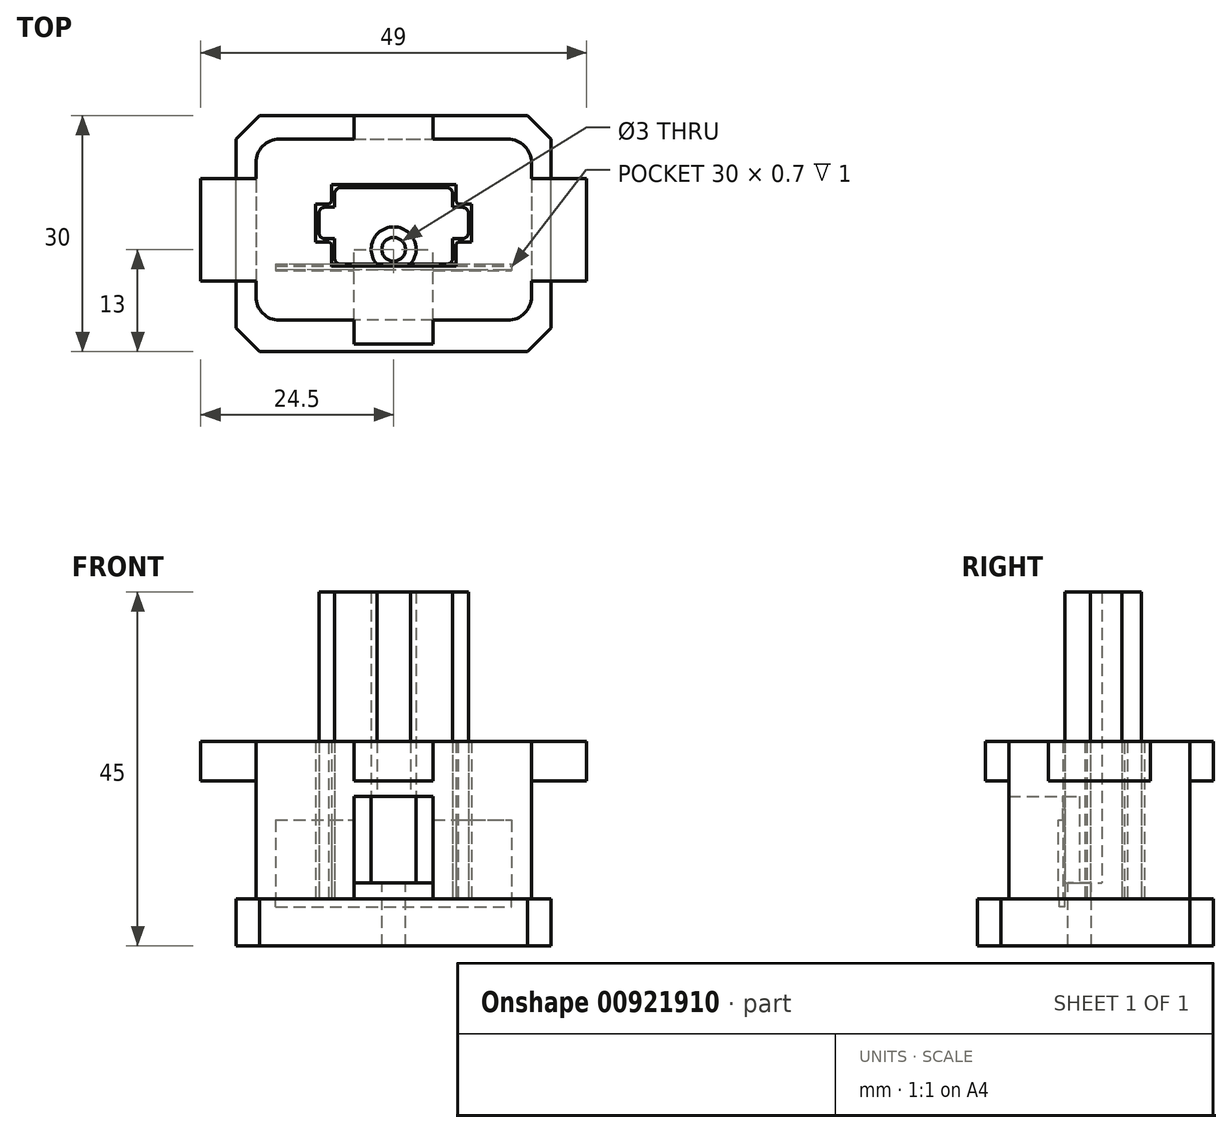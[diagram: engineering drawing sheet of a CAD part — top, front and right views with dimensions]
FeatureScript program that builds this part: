
annotation { "Feature Type Name" : "Feature", "Feature Type Description" : "" }
export const myFeature = defineFeature(function(context is Context, id is Id, definition is map)
    precondition{}
    {
        {
            var Q0;
            Q0=qCreatedBy(makeId("Top.planeOp"),FACE);
            var sketch = newSketch(context, id + "F0", { "sketchPlane" : qUnion([Q0])});
            skLineSegment(sketch, "E0.bottom", {"start": v(-7.5, 7.85) * mm, "end": v(7.5, 7.85) * mm});
            skLineSegment(sketch, "E0.top", {"start": v(-7.5, -1.9) * mm, "end": v(-2.12, -1.9) * mm});
            skLineSegment(sketch, "E0.left", {"start": v(-7.5, 7.85) * mm, "end": v(-7.5, -1.9) * mm});
            skLineSegment(sketch, "E0.right", {"start": v(7.5, 7.85) * mm, "end": v(7.5, -1.9) * mm});
            skArc(sketch, "E1", {"start": v(2.12, -1.9) * mm, "mid": v(0, 2.85) * mm, "end": v(-2.12, -1.9) * mm});
            skLineSegment(sketch, "E2.trimOffspring", {"start": v(2.12, -1.9) * mm, "end": v(7.5, -1.9) * mm});
            skSolve(sketch);
        }
        {
            var Q0;
            Q0=makeQuery(id+"F0.imprint","IMPRINT",FACE,{"disambiguationData":[TD([[makeQuery(id+"F0.imprint","IMPRINT",EDGE,{"derivedFrom":sQuery(id+"F0.wireOp",EDGE,"E0.bottom")}),-1.0]])]});
            extrude(context, id + "F1", {"entities" : qUnion([Q0]), "depth" : 39 * mm, "offsetDistance" : 25 * mm});
        }
        {
            var Q0;
            Q0=makeQuery(id+"F1.opExtrude","CAP_FACE",FACE,{"disambiguationData":[OSD([sQuery(id+"F0.wireOp",EDGE,"E0.bottom"),sQuery(id+"F0.wireOp",EDGE,"E0.top"),sQuery(id+"F0.wireOp",EDGE,"E0.left"),sQuery(id+"F0.wireOp",EDGE,"E0.right"),sQuery(id+"F0.wireOp",EDGE,"E1"),sQuery(id+"F0.wireOp",EDGE,"E2.trimOffspring")])],"isStart":true});
            var sketch = newSketch(context, id + "F2", { "sketchPlane" : qUnion([Q0])});
            skLineSegment(sketch, "E3.bottom", {"start": v(-20, 13) * mm, "end": v(20, 13) * mm});
            skLineSegment(sketch, "E3.top", {"start": v(-20, -17) * mm, "end": v(20, -17) * mm});
            skLineSegment(sketch, "E3.left", {"start": v(-20, 13) * mm, "end": v(-20, -17) * mm});
            skLineSegment(sketch, "E3.right", {"start": v(20, 13) * mm, "end": v(20, -17) * mm});
            skSolve(sketch);
        }
        {
            var Q0;
            Q0 = qSketchRegion(id + "F2", true);
            extrude(context, id + "F3", {"entities" : qUnion([Q0]), "operationType" : NewBodyOperationType.ADD, "depth" : 6 * mm, "offsetDistance" : 25 * mm});
        }
        {
            var Q0;
            Q0=makeQuery(id+"F3.opExtrude","CAP_FACE",FACE,{"disambiguationData":[OSD([sQuery(id+"F2.wireOp",EDGE,"E3.bottom"),sQuery(id+"F2.wireOp",EDGE,"E3.top"),sQuery(id+"F2.wireOp",EDGE,"E3.left"),sQuery(id+"F2.wireOp",EDGE,"E3.right")])],"isStart":true});
            var sketch = newSketch(context, id + "F4", { "sketchPlane" : qUnion([Q0])});
            skLineSegment(sketch, "E4.bottom", {"start": v(-7.5, 5.35) * mm, "end": v(-9.5, 5.35) * mm});
            skLineSegment(sketch, "E4.top", {"start": v(-7.5, 1.35) * mm, "end": v(-9.5, 1.35) * mm});
            skLineSegment(sketch, "E4.left", {"start": v(-7.5, 5.35) * mm, "end": v(-7.5, 1.35) * mm});
            skLineSegment(sketch, "E4.right", {"start": v(-9.5, 5.35) * mm, "end": v(-9.5, 1.35) * mm});
            skLineSegment(sketch, "E5.bottom", {"start": v(7.5, 5.35) * mm, "end": v(9.5, 5.35) * mm});
            skLineSegment(sketch, "E5.top", {"start": v(7.5, 1.35) * mm, "end": v(9.5, 1.35) * mm});
            skLineSegment(sketch, "E5.left", {"start": v(7.5, 5.35) * mm, "end": v(7.5, 1.35) * mm});
            skLineSegment(sketch, "E5.right", {"start": v(9.5, 5.35) * mm, "end": v(9.5, 1.35) * mm});
            skSolve(sketch);
        }
        {
            var Q0;
            Q0 = qSketchRegion(id + "F4", true);
            var Q1;
            Q1=makeQuery(id+"F1.opExtrude","CAP_FACE",FACE,{"disambiguationData":[OSD([sQuery(id+"F0.wireOp",EDGE,"E0.bottom"),sQuery(id+"F0.wireOp",EDGE,"E0.top"),sQuery(id+"F0.wireOp",EDGE,"E0.left"),sQuery(id+"F0.wireOp",EDGE,"E0.right"),sQuery(id+"F0.wireOp",EDGE,"E1"),sQuery(id+"F0.wireOp",EDGE,"E2.trimOffspring")])],"isStart":false});
            extrude(context, id + "F5", {"entities" : qUnion([Q0]), "operationType" : NewBodyOperationType.ADD, "endBound" : BoundingType.UP_TO_SURFACE, "depth" : 25 * mm, "endBoundEntityFace" : qUnion([Q1]), "offsetDistance" : 25 * mm});
        }
        {
            var Q0;
            Q0=makeQuery(id+"F1.opExtrude","SWEPT_EDGE",EDGE,{"disambiguationData":[OSD([sQuery(id+"F0.wireOp",EDGE,"E0.top"),sQuery(id+"F0.wireOp",EDGE,"E0.left")])]});
            var Q1;
            Q1=makeQuery(id+"F1.opExtrude","SWEPT_EDGE",EDGE,{"disambiguationData":[OSD([sQuery(id+"F0.wireOp",EDGE,"E0.right"),sQuery(id+"F0.wireOp",EDGE,"E2.trimOffspring")])]});
            var Q2;
            Q2=makeQuery(id+"F1.opExtrude","SWEPT_EDGE",EDGE,{"disambiguationData":[OSD([sQuery(id+"F0.wireOp",EDGE,"E0.bottom"),sQuery(id+"F0.wireOp",EDGE,"E0.right")])]});
            var Q3;
            Q3=makeQuery(id+"F1.opExtrude","SWEPT_EDGE",EDGE,{"disambiguationData":[OSD([sQuery(id+"F0.wireOp",EDGE,"E0.bottom"),sQuery(id+"F0.wireOp",EDGE,"E0.left")])]});
            var Q4;
            Q4=makeQuery(id+"F5.opExtrude","SWEPT_EDGE",EDGE,{"disambiguationData":[OSD([sQuery(id+"F4.wireOp",EDGE,"E4.bottom"),sQuery(id+"F4.wireOp",EDGE,"E4.right")])]});
            var Q5;
            Q5=makeQuery(id+"F5.opExtrude","SWEPT_EDGE",EDGE,{"disambiguationData":[OSD([sQuery(id+"F4.wireOp",EDGE,"E4.top"),sQuery(id+"F4.wireOp",EDGE,"E4.right")])]});
            var Q6;
            Q6=makeQuery(id+"F5.opExtrude","SWEPT_EDGE",EDGE,{"disambiguationData":[OSD([sQuery(id+"F4.wireOp",EDGE,"E5.top"),sQuery(id+"F4.wireOp",EDGE,"E5.right")])]});
            var Q7;
            Q7=makeQuery(id+"F5.opExtrude","SWEPT_EDGE",EDGE,{"disambiguationData":[OSD([sQuery(id+"F4.wireOp",EDGE,"E5.bottom"),sQuery(id+"F4.wireOp",EDGE,"E5.right")])]});
            fillet(context, id + "F6", {"entities" : qUnion([Q0, Q1, Q2, Q3, Q4, Q5, Q6, Q7]), "radius" : 0.8 * mm, "tangentPropagation" : true, "allowEdgeOverflow" : false});
        }
        {
            var Q0;
            Q0=makeQuery(id+"F3.opExtrude","CAP_FACE",FACE,{"disambiguationData":[OSD([sQuery(id+"F2.wireOp",EDGE,"E3.bottom"),sQuery(id+"F2.wireOp",EDGE,"E3.top"),sQuery(id+"F2.wireOp",EDGE,"E3.left"),sQuery(id+"F2.wireOp",EDGE,"E3.right")])],"isStart":true});
            var sketch = newSketch(context, id + "F7", { "sketchPlane" : qUnion([Q0])});
            skLineSegment(sketch, "E6.bottom", {"start": v(-17.5, 14) * mm, "end": v(17.5, 14) * mm});
            skLineSegment(sketch, "E6.top", {"start": v(-17.5, -9) * mm, "end": v(17.5, -9) * mm});
            skLineSegment(sketch, "E6.left", {"start": v(-17.5, 14) * mm, "end": v(-17.5, -9) * mm});
            skLineSegment(sketch, "E6.right", {"start": v(17.5, 14) * mm, "end": v(17.5, -9) * mm});
            skLineSegment(sketch, "E7.bottom", {"start": v(-7.9, 8.25) * mm, "end": v(7.9, 8.25) * mm});
            skLineSegment(sketch, "E7.top", {"start": v(-7.9, -2.1) * mm, "end": v(7.9, -2.1) * mm});
            skLineSegment(sketch, "E7.left", {"start": v(-9.9, 5.75) * mm, "end": v(-9.9, 0.95) * mm});
            skLineSegment(sketch, "E7.right", {"start": v(9.9, 5.75) * mm, "end": v(9.9, 0.95) * mm});
            skLineSegment(sketch, "E8", {"start": v(-9.9, 5.75) * mm, "end": v(-7.9, 5.75) * mm});
            skLineSegment(sketch, "E9", {"start": v(-7.9, 5.75) * mm, "end": v(-7.9, 8.25) * mm});
            skLineSegment(sketch, "E10.MirrorCS", {"start": v(9.9, 5.75) * mm, "end": v(7.9, 5.75) * mm});
            skLineSegment(sketch, "E11.MirrorCS", {"start": v(7.9, 5.75) * mm, "end": v(7.9, 8.25) * mm});
            skLineSegment(sketch, "E12", {"start": v(-9.9, 0.95) * mm, "end": v(-7.9, 0.95) * mm});
            skLineSegment(sketch, "E13", {"start": v(-7.9, 0.95) * mm, "end": v(-7.9, -2.1) * mm});
            skLineSegment(sketch, "E14.MirrorCS", {"start": v(9.9, 0.95) * mm, "end": v(7.9, 0.95) * mm});
            skLineSegment(sketch, "E15.MirrorCS", {"start": v(7.9, 0.95) * mm, "end": v(7.9, -2.1) * mm});
            skSolve(sketch);
        }
        {
            var Q0;
            Q0 = qSketchRegion(id + "F7", true);
            extrude(context, id + "F8", {"entities" : qUnion([Q0]), "depth" : 20 * mm, "offsetDistance" : 25 * mm});
        }
        {
            var Q0;
            Q0=makeQuery(id+"Fze5ySvmm35KPdi_2.boolean.opBoolean","MERGE",EDGE,{"derivedFrom":[makeQuery(id+"F8.opExtrude","SWEPT_EDGE",EDGE,{"disambiguationData":[OSD([sQuery(id+"F7.wireOp",EDGE,"E6.bottom"),sQuery(id+"F7.wireOp",EDGE,"E6.left")])]}),makeQuery(id+"Fze5ySvmm35KPdi_2.opExtrude","SWEPT_EDGE",EDGE,{"disambiguationData":[OSD([sQuery(id+"F3sfEmMIL337t9d_2.wireOp",EDGE,"Gmu0uAIl-RP7c-kK6N-eZ0a-JbMQpHXrm7wh.bottom"),sQuery(id+"F3sfEmMIL337t9d_2.wireOp",EDGE,"Gmu0uAIl-RP7c-kK6N-eZ0a-JbMQpHXrm7wh.left")])]})]});
            var Q1;
            Q1=makeQuery(id+"Fze5ySvmm35KPdi_2.boolean.opBoolean","MERGE",EDGE,{"derivedFrom":[makeQuery(id+"F8.opExtrude","SWEPT_EDGE",EDGE,{"disambiguationData":[OSD([sQuery(id+"F7.wireOp",EDGE,"E6.bottom"),sQuery(id+"F7.wireOp",EDGE,"E6.right")])]}),makeQuery(id+"Fze5ySvmm35KPdi_2.opExtrude","SWEPT_EDGE",EDGE,{"disambiguationData":[OSD([sQuery(id+"F3sfEmMIL337t9d_2.wireOp",EDGE,"Gmu0uAIl-RP7c-kK6N-eZ0a-JbMQpHXrm7wh.bottom"),sQuery(id+"F3sfEmMIL337t9d_2.wireOp",EDGE,"Gmu0uAIl-RP7c-kK6N-eZ0a-JbMQpHXrm7wh.right")])]})]});
            var Q2;
            Q2=makeQuery(id+"Fze5ySvmm35KPdi_2.boolean.opBoolean","MERGE",EDGE,{"derivedFrom":[makeQuery(id+"F8.opExtrude","SWEPT_EDGE",EDGE,{"disambiguationData":[OSD([sQuery(id+"F7.wireOp",EDGE,"E6.top"),sQuery(id+"F7.wireOp",EDGE,"E6.right")])]}),makeQuery(id+"Fze5ySvmm35KPdi_2.opExtrude","SWEPT_EDGE",EDGE,{"disambiguationData":[OSD([sQuery(id+"F3sfEmMIL337t9d_2.wireOp",EDGE,"Gmu0uAIl-RP7c-kK6N-eZ0a-JbMQpHXrm7wh.top"),sQuery(id+"F3sfEmMIL337t9d_2.wireOp",EDGE,"Gmu0uAIl-RP7c-kK6N-eZ0a-JbMQpHXrm7wh.right")])]})]});
            var Q3;
            Q3=makeQuery(id+"Fze5ySvmm35KPdi_2.boolean.opBoolean","MERGE",EDGE,{"derivedFrom":[makeQuery(id+"F8.opExtrude","SWEPT_EDGE",EDGE,{"disambiguationData":[OSD([sQuery(id+"F7.wireOp",EDGE,"E6.top"),sQuery(id+"F7.wireOp",EDGE,"E6.left")])]}),makeQuery(id+"Fze5ySvmm35KPdi_2.opExtrude","SWEPT_EDGE",EDGE,{"disambiguationData":[OSD([sQuery(id+"F3sfEmMIL337t9d_2.wireOp",EDGE,"Gmu0uAIl-RP7c-kK6N-eZ0a-JbMQpHXrm7wh.top"),sQuery(id+"F3sfEmMIL337t9d_2.wireOp",EDGE,"Gmu0uAIl-RP7c-kK6N-eZ0a-JbMQpHXrm7wh.left")])]})]});
            fillet(context, id + "F9", {"entities" : qUnion([Q0, Q1, Q2, Q3]), "radius" : 3 * mm, "tangentPropagation" : true, "allowEdgeOverflow" : false});
        }
        {
            var Q0;
            Q0=makeQuery(id+"F8.opExtrude","CAP_FACE",FACE,{"disambiguationData":[OSD([sQuery(id+"F7.wireOp",EDGE,"E6.bottom"),sQuery(id+"F7.wireOp",EDGE,"E6.top"),sQuery(id+"F7.wireOp",EDGE,"E6.left"),sQuery(id+"F7.wireOp",EDGE,"E6.right"),sQuery(id+"F7.wireOp",EDGE,"E7.bottom"),sQuery(id+"F7.wireOp",EDGE,"E7.top"),sQuery(id+"F7.wireOp",EDGE,"E7.left"),sQuery(id+"F7.wireOp",EDGE,"E7.right"),sQuery(id+"F7.wireOp",EDGE,"E8"),sQuery(id+"F7.wireOp",EDGE,"E9"),sQuery(id+"F7.wireOp",EDGE,"E10.MirrorCS"),sQuery(id+"F7.wireOp",EDGE,"E11.MirrorCS"),sQuery(id+"F7.wireOp",EDGE,"E12"),sQuery(id+"F7.wireOp",EDGE,"E13"),sQuery(id+"F7.wireOp",EDGE,"E14.MirrorCS"),sQuery(id+"F7.wireOp",EDGE,"E15.MirrorCS")])],"isStart":false});
            var sketch = newSketch(context, id + "F10", { "sketchPlane" : qUnion([Q0])});
            skLineSegment(sketch, "E16.bottom", {"start": v(-5, 14) * mm, "end": v(5, 14) * mm});
            skLineSegment(sketch, "E16.top", {"start": v(-5, 17) * mm, "end": v(5, 17) * mm});
            skLineSegment(sketch, "E16.left", {"start": v(-5, 14) * mm, "end": v(-5, 17) * mm});
            skLineSegment(sketch, "E16.right", {"start": v(5, 14) * mm, "end": v(5, 17) * mm});
            skLineSegment(sketch, "E17.bottom", {"start": v(-5, -9) * mm, "end": v(5, -9) * mm});
            skLineSegment(sketch, "E17.top", {"start": v(-5, -12) * mm, "end": v(5, -12) * mm});
            skLineSegment(sketch, "E17.left", {"start": v(-5, -9) * mm, "end": v(-5, -12) * mm});
            skLineSegment(sketch, "E17.right", {"start": v(5, -9) * mm, "end": v(5, -12) * mm});
            skSolve(sketch);
        }
        {
            var Q0;
            Q0 = qSketchRegion(id + "F10", true);
            extrude(context, id + "F11", {"entities" : qUnion([Q0]), "operationType" : NewBodyOperationType.ADD, "oppositeDirection" : true, "depth" : 5 * mm, "offsetDistance" : 25 * mm});
        }
        {
            var Q0;
            Q0=makeQuery(id+"F3.opExtrude","SWEPT_EDGE",EDGE,{"disambiguationData":[OSD([sQuery(id+"F2.wireOp",EDGE,"E3.bottom"),sQuery(id+"F2.wireOp",EDGE,"E3.left")])]});
            var Q1;
            Q1=makeQuery(id+"F3.opExtrude","SWEPT_EDGE",EDGE,{"disambiguationData":[OSD([sQuery(id+"F2.wireOp",EDGE,"E3.bottom"),sQuery(id+"F2.wireOp",EDGE,"E3.right")])]});
            var Q2;
            Q2=makeQuery(id+"F3.opExtrude","SWEPT_EDGE",EDGE,{"disambiguationData":[OSD([sQuery(id+"F2.wireOp",EDGE,"E3.top"),sQuery(id+"F2.wireOp",EDGE,"E3.right")])]});
            var Q3;
            Q3=makeQuery(id+"F3.opExtrude","SWEPT_EDGE",EDGE,{"disambiguationData":[OSD([sQuery(id+"F2.wireOp",EDGE,"E3.top"),sQuery(id+"F2.wireOp",EDGE,"E3.left")])]});
            chamfer(context, id + "F12", {"entities" : qUnion([Q0, Q1, Q2, Q3]), "width" : 3 * mm, "tangentPropagation" : true});
        }
        {
            var Q0;
            Q0=makeQuery(id+"F8.opExtrude","CAP_FACE",FACE,{"disambiguationData":[OSD([sQuery(id+"F7.wireOp",EDGE,"E6.bottom"),sQuery(id+"F7.wireOp",EDGE,"E6.top"),sQuery(id+"F7.wireOp",EDGE,"E6.left"),sQuery(id+"F7.wireOp",EDGE,"E6.right"),sQuery(id+"F7.wireOp",EDGE,"E7.bottom"),sQuery(id+"F7.wireOp",EDGE,"E7.top"),sQuery(id+"F7.wireOp",EDGE,"E7.left"),sQuery(id+"F7.wireOp",EDGE,"E7.right"),sQuery(id+"F7.wireOp",EDGE,"E8"),sQuery(id+"F7.wireOp",EDGE,"E9"),sQuery(id+"F7.wireOp",EDGE,"E10.MirrorCS"),sQuery(id+"F7.wireOp",EDGE,"E11.MirrorCS"),sQuery(id+"F7.wireOp",EDGE,"E12"),sQuery(id+"F7.wireOp",EDGE,"E13"),sQuery(id+"F7.wireOp",EDGE,"E14.MirrorCS"),sQuery(id+"F7.wireOp",EDGE,"E15.MirrorCS")])],"isStart":true});
            var sketch = newSketch(context, id + "F13", { "sketchPlane" : qUnion([Q0])});
            skLineSegment(sketch, "E18.bottom", {"start": v(-15, 2.1) * mm, "end": v(15, 2.1) * mm});
            skLineSegment(sketch, "E18.top", {"start": v(-15, 2.7) * mm, "end": v(15, 2.7) * mm});
            skLineSegment(sketch, "E18.left", {"start": v(-15, 2.1) * mm, "end": v(-15, 2.7) * mm});
            skLineSegment(sketch, "E18.right", {"start": v(15, 2.1) * mm, "end": v(15, 2.7) * mm});
            skSolve(sketch);
        }
        {
            var Q0;
            Q0 = qSketchRegion(id + "F13", true);
            extrude(context, id + "F14", {"entities" : qUnion([Q0]), "operationType" : NewBodyOperationType.REMOVE, "oppositeDirection" : true, "depth" : 10 * mm, "offsetDistance" : 25 * mm});
        }
        {
            var Q0;
            Q0=makeQuery(id+"F8.opExtrude","CAP_FACE",FACE,{"disambiguationData":[OSD([sQuery(id+"F7.wireOp",EDGE,"E6.bottom"),sQuery(id+"F7.wireOp",EDGE,"E6.top"),sQuery(id+"F7.wireOp",EDGE,"E6.left"),sQuery(id+"F7.wireOp",EDGE,"E6.right"),sQuery(id+"F7.wireOp",EDGE,"E7.bottom"),sQuery(id+"F7.wireOp",EDGE,"E7.top"),sQuery(id+"F7.wireOp",EDGE,"E7.left"),sQuery(id+"F7.wireOp",EDGE,"E7.right"),sQuery(id+"F7.wireOp",EDGE,"E8"),sQuery(id+"F7.wireOp",EDGE,"E9"),sQuery(id+"F7.wireOp",EDGE,"E10.MirrorCS"),sQuery(id+"F7.wireOp",EDGE,"E11.MirrorCS"),sQuery(id+"F7.wireOp",EDGE,"E12"),sQuery(id+"F7.wireOp",EDGE,"E13"),sQuery(id+"F7.wireOp",EDGE,"E14.MirrorCS"),sQuery(id+"F7.wireOp",EDGE,"E15.MirrorCS")])],"isStart":true});
            var sketch = newSketch(context, id + "F15", { "sketchPlane" : qUnion([Q0])});
            skLineSegment(sketch, "E19.bottom", {"start": v(-5, 15) * mm, "end": v(5, 15) * mm});
            skLineSegment(sketch, "E19.top", {"start": v(-5, 0) * mm, "end": v(5, 0) * mm});
            skLineSegment(sketch, "E19.left", {"start": v(-5, 15) * mm, "end": v(-5, 0) * mm});
            skLineSegment(sketch, "E19.right", {"start": v(5, 15) * mm, "end": v(5, 0) * mm});
            skSolve(sketch);
        }
        {
            var Q0;
            Q0 = qSketchRegion(id + "F15", true);
            extrude(context, id + "F16", {"entities" : qUnion([Q0]), "operationType" : NewBodyOperationType.REMOVE, "oppositeDirection" : true, "depth" : 13 * mm, "offsetDistance" : 25 * mm});
        }
        {
            var Q0;
            Q0=makeQuery(id+"F3.opExtrude","CAP_FACE",FACE,{"disambiguationData":[OSD([sQuery(id+"F2.wireOp",EDGE,"E3.bottom"),sQuery(id+"F2.wireOp",EDGE,"E3.top"),sQuery(id+"F2.wireOp",EDGE,"E3.left"),sQuery(id+"F2.wireOp",EDGE,"E3.right")])],"isStart":true});
            var sketch = newSketch(context, id + "F17", { "sketchPlane" : qUnion([Q0])});
            skLineSegment(sketch, "E20.bottom", {"start": v(-15, -1.9) * mm, "end": v(15, -1.9) * mm});
            skLineSegment(sketch, "E20.top", {"start": v(-15, -2.6) * mm, "end": v(15, -2.6) * mm});
            skLineSegment(sketch, "E20.left", {"start": v(-15, -1.9) * mm, "end": v(-15, -2.6) * mm});
            skLineSegment(sketch, "E20.right", {"start": v(15, -1.9) * mm, "end": v(15, -2.6) * mm});
            skSolve(sketch);
        }
        {
            var Q0;
            Q0 = qSketchRegion(id + "F17", true);
            extrude(context, id + "F18", {"entities" : qUnion([Q0]), "operationType" : NewBodyOperationType.REMOVE, "oppositeDirection" : true, "depth" : 1 * mm, "offsetDistance" : 25 * mm});
        }
        {
            var Q0;
            Q0=makeQuery(id+"F18.boolean.opBoolean","SPLIT",FACE,{"disambiguationData":[TD([makeQuery(id+"F1.opExtrude","SWEPT_FACE",FACE,{"disambiguationData":[OSD([sQuery(id+"F0.wireOp",EDGE,"E1")])]})])],"derivedFrom":makeQuery(id+"F3.opExtrude","CAP_FACE",FACE,{"disambiguationData":[OSD([sQuery(id+"F2.wireOp",EDGE,"E3.bottom"),sQuery(id+"F2.wireOp",EDGE,"E3.top"),sQuery(id+"F2.wireOp",EDGE,"E3.left"),sQuery(id+"F2.wireOp",EDGE,"E3.right")])],"isStart":true})});
            extrude(context, id + "F19", {"entities" : qUnion([Q0]), "operationType" : NewBodyOperationType.ADD, "depth" : 2 * mm, "offsetDistance" : 25 * mm});
        }
        {
            var Q0;
            Q0=makeQuery(id+"F19.opExtrude","CAP_FACE",FACE,{"disambiguationData":[OSD([sQuery(id+"F2.wireOp",EDGE,"E3.bottom"),sQuery(id+"F2.wireOp",EDGE,"E3.top"),sQuery(id+"F2.wireOp",EDGE,"E3.left"),sQuery(id+"F2.wireOp",EDGE,"E3.right")])],"isStart":false});
            var sketch = newSketch(context, id + "F20", { "sketchPlane" : qUnion([Q0])});
            skCircle(sketch, "E21", {"center": v(0, 0) * mm, "radius": 1.5 * mm});
            skSolve(sketch);
        }
        {
            var Q0;
            Q0 = qSketchRegion(id + "F20", true);
            extrude(context, id + "F21", {"entities" : qUnion([Q0]), "operationType" : NewBodyOperationType.REMOVE, "oppositeDirection" : true, "depth" : 25 * mm, "offsetDistance" : 25 * mm});
        }
        {
            var Q0;
            Q0=makeQuery(id+"F11.boolean.opBoolean","MERGE",FACE,{"derivedFrom":[makeQuery(id+"F8.opExtrude","CAP_FACE",FACE,{"disambiguationData":[OSD([sQuery(id+"F7.wireOp",EDGE,"E6.bottom"),sQuery(id+"F7.wireOp",EDGE,"E6.top"),sQuery(id+"F7.wireOp",EDGE,"E6.left"),sQuery(id+"F7.wireOp",EDGE,"E6.right"),sQuery(id+"F7.wireOp",EDGE,"E7.bottom"),sQuery(id+"F7.wireOp",EDGE,"E7.top"),sQuery(id+"F7.wireOp",EDGE,"E7.left"),sQuery(id+"F7.wireOp",EDGE,"E7.right"),sQuery(id+"F7.wireOp",EDGE,"E8"),sQuery(id+"F7.wireOp",EDGE,"E9"),sQuery(id+"F7.wireOp",EDGE,"E10.MirrorCS"),sQuery(id+"F7.wireOp",EDGE,"E11.MirrorCS"),sQuery(id+"F7.wireOp",EDGE,"E12"),sQuery(id+"F7.wireOp",EDGE,"E13"),sQuery(id+"F7.wireOp",EDGE,"E14.MirrorCS"),sQuery(id+"F7.wireOp",EDGE,"E15.MirrorCS")])],"isStart":false}),makeQuery(id+"F11.opExtrude","CAP_FACE",FACE,{"disambiguationData":[OSD([sQuery(id+"F10.wireOp",EDGE,"E16.bottom"),sQuery(id+"F10.wireOp",EDGE,"E16.top"),sQuery(id+"F10.wireOp",EDGE,"E16.left"),sQuery(id+"F10.wireOp",EDGE,"E16.right")])],"isStart":true}),makeQuery(id+"F11.opExtrude","CAP_FACE",FACE,{"disambiguationData":[OSD([sQuery(id+"F10.wireOp",EDGE,"E17.bottom"),sQuery(id+"F10.wireOp",EDGE,"E17.top"),sQuery(id+"F10.wireOp",EDGE,"E17.left"),sQuery(id+"F10.wireOp",EDGE,"E17.right")])],"isStart":true})]});
            var sketch = newSketch(context, id + "F22", { "sketchPlane" : qUnion([Q0])});
            skLineSegment(sketch, "E22.bottom", {"start": v(-17.5, 9) * mm, "end": v(-24.5, 9) * mm});
            skLineSegment(sketch, "E22.top", {"start": v(-17.5, -4) * mm, "end": v(-24.5, -4) * mm});
            skLineSegment(sketch, "E22.left", {"start": v(-17.5, 9) * mm, "end": v(-17.5, -4) * mm});
            skLineSegment(sketch, "E22.right", {"start": v(-24.5, 9) * mm, "end": v(-24.5, -4) * mm});
            skLineSegment(sketch, "E23.MirrorCS", {"start": v(17.5, -4) * mm, "end": v(24.5, -4) * mm});
            skLineSegment(sketch, "E24.MirrorCS", {"start": v(24.5, 9) * mm, "end": v(24.5, -4) * mm});
            skLineSegment(sketch, "E25.MirrorCS", {"start": v(17.5, 9) * mm, "end": v(24.5, 9) * mm});
            skLineSegment(sketch, "E26.MirrorCS", {"start": v(17.5, 9) * mm, "end": v(17.5, -4) * mm});
            skSolve(sketch);
        }
        {
            var Q0;
            Q0 = qSketchRegion(id + "F22", true);
            extrude(context, id + "F23", {"entities" : qUnion([Q0]), "operationType" : NewBodyOperationType.ADD, "oppositeDirection" : true, "depth" : 5 * mm, "offsetDistance" : 25 * mm});
        }
        {
            var Q0;
            Q0=makeQuery(id+"F8.opExtrude","SWEPT_EDGE",EDGE,{"disambiguationData":[OSD([sQuery(id+"F7.wireOp",EDGE,"E8"),sQuery(id+"F7.wireOp",EDGE,"E9")])]});
            var Q1;
            Q1=makeQuery(id+"F8.opExtrude","SWEPT_EDGE",EDGE,{"disambiguationData":[OSD([sQuery(id+"F7.wireOp",EDGE,"E10.MirrorCS"),sQuery(id+"F7.wireOp",EDGE,"E11.MirrorCS")])]});
            var Q2;
            Q2=makeQuery(id+"F8.opExtrude","SWEPT_EDGE",EDGE,{"disambiguationData":[OSD([sQuery(id+"F7.wireOp",EDGE,"E12"),sQuery(id+"F7.wireOp",EDGE,"E13")])]});
            var Q3;
            Q3=makeQuery(id+"F8.opExtrude","SWEPT_EDGE",EDGE,{"disambiguationData":[OSD([sQuery(id+"F7.wireOp",EDGE,"E14.MirrorCS"),sQuery(id+"F7.wireOp",EDGE,"E15.MirrorCS")])]});
            chamfer(context, id + "F24", {"entities" : qUnion([Q0, Q1, Q2, Q3]), "width" : 0.3 * mm, "tangentPropagation" : true});
        }
    });
